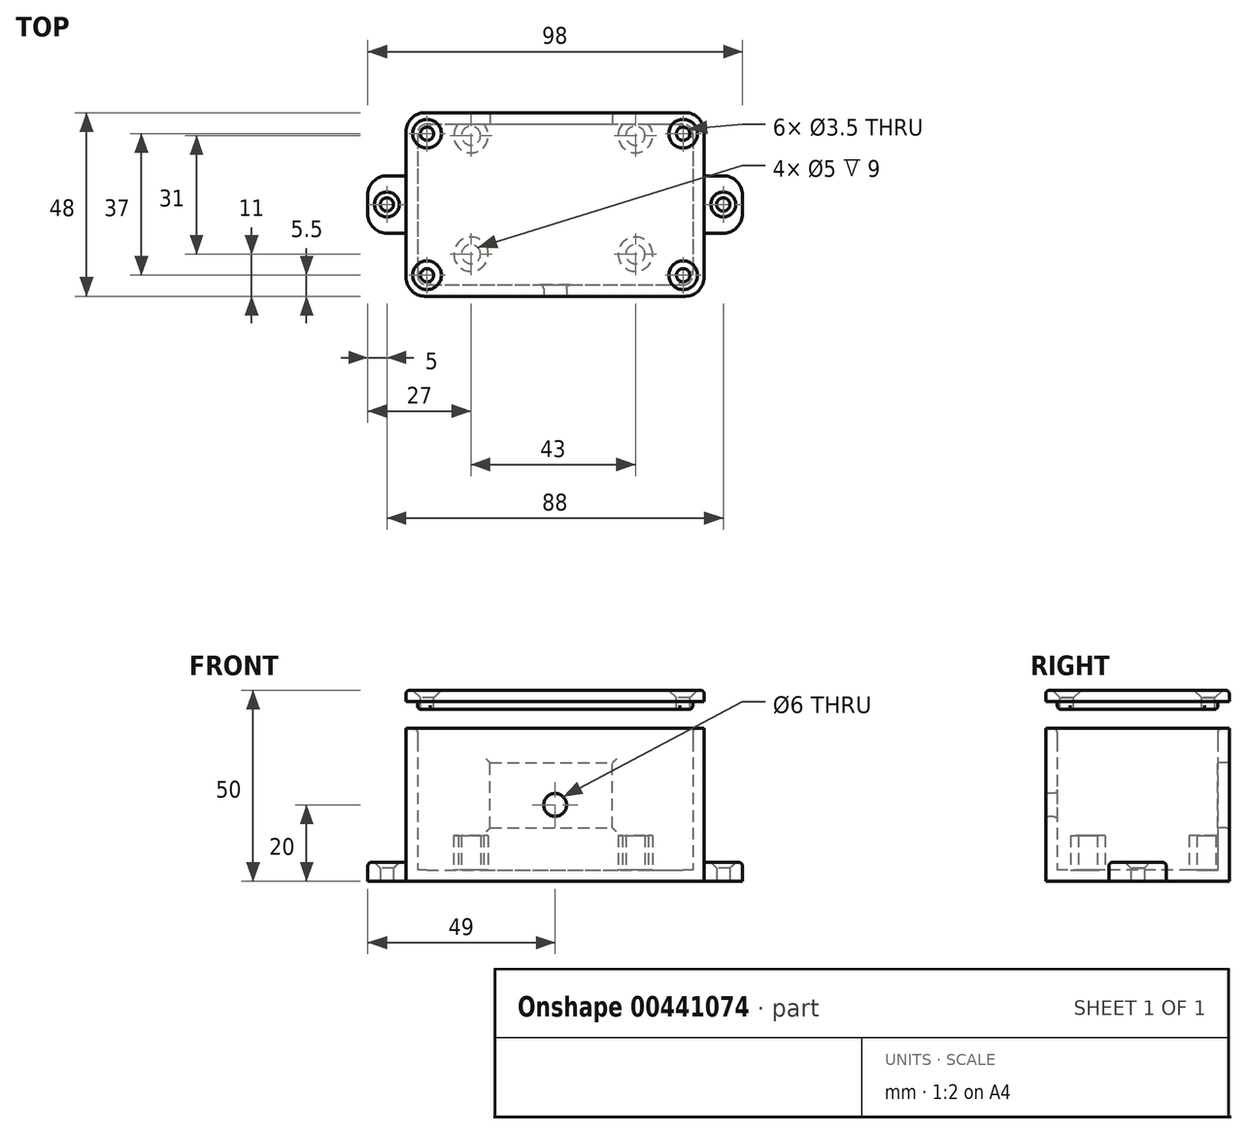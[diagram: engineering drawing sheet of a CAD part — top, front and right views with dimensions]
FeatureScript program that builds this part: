
annotation { "Feature Type Name" : "Feature", "Feature Type Description" : "" }
export const myFeature = defineFeature(function(context is Context, id is Id, definition is map)
    precondition{}
    {
        {
            var Q0;
            Q0=qCreatedBy(makeId("Top.planeOp"),FACE);
            var sketch = newSketch(context, id + "F0", { "sketchPlane" : qUnion([Q0])});
            skLineSegment(sketch, "E0.bottom", {"start": v(-36, 21) * mm, "end": v(36, 21) * mm});
            skLineSegment(sketch, "E0.top", {"start": v(-36, -21) * mm, "end": v(36, -21) * mm});
            skLineSegment(sketch, "E0.left", {"start": v(-36, 21) * mm, "end": v(-36, -21) * mm});
            skLineSegment(sketch, "E0.right", {"start": v(36, 21) * mm, "end": v(36, -21) * mm});
            skLineSegment(sketch, "E1.0", {"start": v(-39, 24) * mm, "end": v(39, 24) * mm});
            skLineSegment(sketch, "E1.1", {"start": v(-39, 24) * mm, "end": v(-39, -24) * mm});
            skLineSegment(sketch, "E1.2", {"start": v(-39, -24) * mm, "end": v(39, -24) * mm});
            skLineSegment(sketch, "E1.3", {"start": v(39, 24) * mm, "end": v(39, -24) * mm});
            skLineSegment(sketch, "E2.bottom", {"start": v(39, 7.5) * mm, "end": v(49, 7.5) * mm});
            skLineSegment(sketch, "E2.top", {"start": v(39, -7.5) * mm, "end": v(49, -7.5) * mm});
            skLineSegment(sketch, "E2.left", {"start": v(39, 7.5) * mm, "end": v(39, -7.5) * mm});
            skLineSegment(sketch, "E2.right", {"start": v(49, 7.5) * mm, "end": v(49, -7.5) * mm});
            skLineSegment(sketch, "E3.bottom", {"start": v(-39, -7.5) * mm, "end": v(-49, -7.5) * mm});
            skLineSegment(sketch, "E3.top", {"start": v(-39, 7.5) * mm, "end": v(-49, 7.5) * mm});
            skLineSegment(sketch, "E3.left", {"start": v(-39, -7.5) * mm, "end": v(-39, 7.5) * mm});
            skLineSegment(sketch, "E3.right", {"start": v(-49, -7.5) * mm, "end": v(-49, 7.5) * mm});
            skCircle(sketch, "E4", {"center": v(44, 0) * mm, "radius": 1.75 * mm});
            skCircle(sketch, "E5", {"center": v(-44, 0) * mm, "radius": 1.75 * mm});
            skSolve(sketch);
        }
        {
            var Q0;
            Q0=makeQuery(id+"F0.imprint","IMPRINT",FACE,{"disambiguationData":[TD([[makeQuery(id+"F0.imprint","IMPRINT",EDGE,{"derivedFrom":sQuery(id+"F0.wireOp",EDGE,"E0.bottom")}),1.0]])]});
            extrude(context, id + "F1", {"entities" : qUnion([Q0]), "depth" : 40 * mm});
        }
        {
            var Q0;
            Q0=makeQuery(id+"F0.imprint","IMPRINT",FACE,{"disambiguationData":[TD([[makeQuery(id+"F0.imprint","IMPRINT",EDGE,{"derivedFrom":sQuery(id+"F0.wireOp",EDGE,"E0.bottom")}),-1.0]])]});
            extrude(context, id + "F2", {"entities" : qUnion([Q0]), "operationType" : NewBodyOperationType.ADD, "depth" : 3 * mm});
        }
        {
            var Q0;
            Q0=makeQuery(id+"F2.opExtrude","CAP_FACE",FACE,{"disambiguationData":[OSD([sQuery(id+"F0.wireOp",EDGE,"E0.bottom"),sQuery(id+"F0.wireOp",EDGE,"E0.top"),sQuery(id+"F0.wireOp",EDGE,"E0.left"),sQuery(id+"F0.wireOp",EDGE,"E0.right")])],"isStart":false});
            var sketch = newSketch(context, id + "F3", { "sketchPlane" : qUnion([Q0])});
            skCircle(sketch, "E6", {"center": v(-22, 18) * mm, "radius": 4.5 * mm});
            skCircle(sketch, "E7", {"center": v(21, 18) * mm, "radius": 4.5 * mm});
            skCircle(sketch, "E8", {"center": v(-22, -13) * mm, "radius": 4.5 * mm});
            skCircle(sketch, "E9", {"center": v(21, -13) * mm, "radius": 4.5 * mm});
            skCircle(sketch, "E10", {"center": v(-22, 18) * mm, "radius": 2.5 * mm});
            skCircle(sketch, "E11", {"center": v(21, 18) * mm, "radius": 2.5 * mm});
            skCircle(sketch, "E12", {"center": v(-22, -13) * mm, "radius": 2.5 * mm});
            skCircle(sketch, "E13", {"center": v(21, -13) * mm, "radius": 2.5 * mm});
            skCircle(sketch, "E14", {"center": v(-33.5, 18.5) * mm, "radius": 2.5 * mm});
            skCircle(sketch, "E15", {"center": v(-33.5, -18.5) * mm, "radius": 2.5 * mm});
            skCircle(sketch, "E16", {"center": v(33.5, -18.5) * mm, "radius": 2.5 * mm});
            skCircle(sketch, "E17", {"center": v(33.5, 18.5) * mm, "radius": 2.5 * mm});
            skCircle(sketch, "E18", {"center": v(-33.5, 18.5) * mm, "radius": 5.5 * mm});
            skCircle(sketch, "E19", {"center": v(33.5, 18.5) * mm, "radius": 5.5 * mm});
            skCircle(sketch, "E20", {"center": v(33.5, -18.5) * mm, "radius": 5.5 * mm});
            skCircle(sketch, "E21", {"center": v(-33.5, -18.5) * mm, "radius": 5.5 * mm});
            skSolve(sketch);
        }
        {
            var Q0;
            Q0=makeQuery(id+"F3.imprint","IMPRINT",FACE,{"disambiguationData":[TD([[makeQuery(id+"F3.imprint","IMPRINT",EDGE,{"derivedFrom":sQuery(id+"F3.wireOp",EDGE,"E10")}),-1.0]])]});
            var Q1;
            Q1=makeQuery(id+"F3.imprint","IMPRINT",FACE,{"disambiguationData":[TD([[makeQuery(id+"F3.imprint","IMPRINT",EDGE,{"derivedFrom":sQuery(id+"F3.wireOp",EDGE,"E8")}),1.0]])]});
            var Q2;
            Q2=makeQuery(id+"F3.imprint","IMPRINT",FACE,{"disambiguationData":[TD([[makeQuery(id+"F3.imprint","IMPRINT",EDGE,{"derivedFrom":sQuery(id+"F3.wireOp",EDGE,"E9")}),1.0]])]});
            var Q3;
            Q3=makeQuery(id+"F3.imprint","IMPRINT",FACE,{"disambiguationData":[TD([[makeQuery(id+"F3.imprint","IMPRINT",EDGE,{"derivedFrom":sQuery(id+"F3.wireOp",EDGE,"E11")}),-1.0]])]});
            var Q4;
            Q4=makeQuery(id+"F3.imprint","IMPRINT",FACE,{"disambiguationData":[TD([[makeQuery(id+"F3.imprint","IMPRINT",EDGE,{"derivedFrom":sQuery(id+"F3.wireOp",EDGE,"E12")}),-1.0]])]});
            extrude(context, id + "F4", {"entities" : qUnion([Q0, Q1, Q2, Q3, Q4]), "operationType" : NewBodyOperationType.ADD, "depth" : 9 * mm});
        }
        {
            var Q0;
            Q0=makeQuery(id+"F1.opExtrude","SWEPT_FACE",FACE,{"disambiguationData":[OSD([sQuery(id+"F0.wireOp",EDGE,"E0.bottom")])]});
            var sketch = newSketch(context, id + "F5", { "sketchPlane" : qUnion([Q0])});
            skLineSegment(sketch, "E22.bottom", {"start": v(-17, 14) * mm, "end": v(15, 14) * mm});
            skLineSegment(sketch, "E22.top", {"start": v(-17, 31) * mm, "end": v(15, 31) * mm});
            skLineSegment(sketch, "E22.left", {"start": v(-17, 14) * mm, "end": v(-17, 31) * mm});
            skLineSegment(sketch, "E22.right", {"start": v(15, 14) * mm, "end": v(15, 31) * mm});
            skSolve(sketch);
        }
        {
            var Q0;
            Q0=makeQuery(id+"F5.imprint","IMPRINT",FACE,{"disambiguationData":[TD([[makeQuery(id+"F5.imprint","IMPRINT",EDGE,{"derivedFrom":sQuery(id+"F5.wireOp",EDGE,"E22.bottom")}),1.0]])]});
            extrude(context, id + "F6", {"entities" : qUnion([Q0]), "operationType" : NewBodyOperationType.REMOVE, "oppositeDirection" : true, "depth" : 25 * mm});
        }
        {
            var Q0;
            {var subQ0=sQuery(id+"F3.wireOp",EDGE,"E15");var subQ1=makeQuery(id+"F2.opExtrude","CAP_EDGE",EDGE,{"disambiguationData":[OSD([sQuery(id+"F0.wireOp",EDGE,"E0.top")])],"isStart":false});var subQ2=makeQuery(id+"F3.imprint","INTERSECT",VERTEX,{"derivedFrom":[subQ1,subQ0]});Q0=makeQuery(id+"F3.imprint","IMPRINT",FACE,{"disambiguationData":[TD([[makeQuery(id+"F3.imprint","IMPRINT",EDGE,{"disambiguationData":[TD([[subQ2,-1.0]])],"derivedFrom":subQ0}),-1.0]])]});}
            var Q1;
            {var subQ0=sQuery(id+"F3.wireOp",EDGE,"E16");var subQ1=makeQuery(id+"F2.opExtrude","CAP_EDGE",EDGE,{"disambiguationData":[OSD([sQuery(id+"F0.wireOp",EDGE,"E0.top")])],"isStart":false});var subQ2=makeQuery(id+"F3.imprint","INTERSECT",VERTEX,{"derivedFrom":[subQ1,subQ0]});Q1=makeQuery(id+"F3.imprint","IMPRINT",FACE,{"disambiguationData":[TD([[makeQuery(id+"F3.imprint","IMPRINT",EDGE,{"disambiguationData":[TD([[subQ2,1.0]])],"derivedFrom":subQ0}),-1.0]])]});}
            var Q2;
            {var subQ0=sQuery(id+"F3.wireOp",EDGE,"E17");var subQ1=makeQuery(id+"F2.opExtrude","CAP_EDGE",EDGE,{"disambiguationData":[OSD([sQuery(id+"F0.wireOp",EDGE,"E0.bottom")])],"isStart":false});var subQ2=makeQuery(id+"F3.imprint","INTERSECT",VERTEX,{"derivedFrom":[subQ1,subQ0]});Q2=makeQuery(id+"F3.imprint","IMPRINT",FACE,{"disambiguationData":[TD([[makeQuery(id+"F3.imprint","IMPRINT",EDGE,{"disambiguationData":[TD([[subQ2,-1.0]])],"derivedFrom":subQ0}),-1.0]])]});}
            var Q3;
            {var subQ0=sQuery(id+"F3.wireOp",EDGE,"E14");var subQ1=makeQuery(id+"F2.opExtrude","CAP_EDGE",EDGE,{"disambiguationData":[OSD([sQuery(id+"F0.wireOp",EDGE,"E0.bottom")])],"isStart":false});var subQ2=makeQuery(id+"F3.imprint","INTERSECT",VERTEX,{"derivedFrom":[subQ1,subQ0]});Q3=makeQuery(id+"F3.imprint","IMPRINT",FACE,{"disambiguationData":[TD([[makeQuery(id+"F3.imprint","IMPRINT",EDGE,{"disambiguationData":[TD([[subQ2,1.0]])],"derivedFrom":subQ0}),-1.0]])]});}
            extrude(context, id + "F7", {"entities" : qUnion([Q0, Q1, Q2, Q3]), "operationType" : NewBodyOperationType.ADD, "depth" : 34 * mm});
        }
        {
            var Q0;
            Q0=makeQuery(id+"F1.opExtrude","SWEPT_EDGE",EDGE,{"disambiguationData":[OSD([sQuery(id+"F0.wireOp",EDGE,"E1.1"),sQuery(id+"F0.wireOp",EDGE,"E1.2")])]});
            var Q1;
            Q1=makeQuery(id+"F1.opExtrude","SWEPT_EDGE",EDGE,{"disambiguationData":[OSD([sQuery(id+"F0.wireOp",EDGE,"E1.2"),sQuery(id+"F0.wireOp",EDGE,"E1.3")])]});
            var Q2;
            Q2=makeQuery(id+"F1.opExtrude","SWEPT_EDGE",EDGE,{"disambiguationData":[OSD([sQuery(id+"F0.wireOp",EDGE,"E1.0"),sQuery(id+"F0.wireOp",EDGE,"E1.3")])]});
            var Q3;
            Q3=makeQuery(id+"F1.opExtrude","SWEPT_EDGE",EDGE,{"disambiguationData":[OSD([sQuery(id+"F0.wireOp",EDGE,"E1.0"),sQuery(id+"F0.wireOp",EDGE,"E1.1")])]});
            fillet(context, id + "F8", {"entities" : qUnion([Q0, Q1, Q2, Q3]), "radius" : 5 * mm, "tangentPropagation" : true, "allowEdgeOverflow" : false});
        }
        {
            var Q0;
            Q0=makeQuery(id+"F1.opExtrude","SWEPT_EDGE",EDGE,{"disambiguationData":[OSD([sQuery(id+"F0.wireOp",EDGE,"E0.top"),sQuery(id+"F0.wireOp",EDGE,"E0.left")])]});
            var Q1;
            Q1=makeQuery(id+"F1.opExtrude","SWEPT_EDGE",EDGE,{"disambiguationData":[OSD([sQuery(id+"F0.wireOp",EDGE,"E0.bottom"),sQuery(id+"F0.wireOp",EDGE,"E0.left")])]});
            var Q2;
            Q2=makeQuery(id+"F1.opExtrude","SWEPT_EDGE",EDGE,{"disambiguationData":[OSD([sQuery(id+"F0.wireOp",EDGE,"E0.top"),sQuery(id+"F0.wireOp",EDGE,"E0.right")])]});
            var Q3;
            Q3=makeQuery(id+"F1.opExtrude","SWEPT_EDGE",EDGE,{"disambiguationData":[OSD([sQuery(id+"F0.wireOp",EDGE,"E0.bottom"),sQuery(id+"F0.wireOp",EDGE,"E0.right")])]});
            fillet(context, id + "F9", {"entities" : qUnion([Q0, Q1, Q2, Q3]), "radius" : 2.5 * mm, "tangentPropagation" : true, "allowEdgeOverflow" : false});
        }
        {
            var Q0;
            Q0=makeQuery(id+"F6.boolean.opBoolean","INTERSECT",EDGE,{"derivedFrom":[makeQuery(id+"F1.opExtrude","SWEPT_FACE",FACE,{"disambiguationData":[OSD([sQuery(id+"F0.wireOp",EDGE,"E1.0")])]}),makeQuery(id+"F6.opExtrude","SWEPT_FACE",FACE,{"disambiguationData":[OSD([sQuery(id+"F5.wireOp",EDGE,"E22.top")])]})]});
            var Q1;
            Q1=makeQuery(id+"F6.boolean.opBoolean","INTERSECT",EDGE,{"derivedFrom":[makeQuery(id+"F1.opExtrude","SWEPT_FACE",FACE,{"disambiguationData":[OSD([sQuery(id+"F0.wireOp",EDGE,"E1.0")])]}),makeQuery(id+"F6.opExtrude","SWEPT_FACE",FACE,{"disambiguationData":[OSD([sQuery(id+"F5.wireOp",EDGE,"E22.left")])]})]});
            var Q2;
            Q2=makeQuery(id+"F6.boolean.opBoolean","INTERSECT",EDGE,{"derivedFrom":[makeQuery(id+"F1.opExtrude","SWEPT_FACE",FACE,{"disambiguationData":[OSD([sQuery(id+"F0.wireOp",EDGE,"E1.0")])]}),makeQuery(id+"F6.opExtrude","SWEPT_FACE",FACE,{"disambiguationData":[OSD([sQuery(id+"F5.wireOp",EDGE,"E22.bottom")])]})]});
            var Q3;
            Q3=makeQuery(id+"F6.boolean.opBoolean","INTERSECT",EDGE,{"derivedFrom":[makeQuery(id+"F1.opExtrude","SWEPT_FACE",FACE,{"disambiguationData":[OSD([sQuery(id+"F0.wireOp",EDGE,"E1.0")])]}),makeQuery(id+"F6.opExtrude","SWEPT_FACE",FACE,{"disambiguationData":[OSD([sQuery(id+"F5.wireOp",EDGE,"E22.right")])]})]});
            fillet(context, id + "F10", {"entities" : qUnion([Q0, Q1, Q2, Q3]), "radius" : 1 * mm, "tangentPropagation" : true, "allowEdgeOverflow" : false});
        }
        {
            var Q0;
            Q0=makeQuery(id+"F0.imprint","IMPRINT",FACE,{"disambiguationData":[TD([[makeQuery(id+"F0.imprint","IMPRINT",EDGE,{"derivedFrom":sQuery(id+"F0.wireOp",EDGE,"E2.bottom")}),-1.0]])]});
            var Q1;
            Q1=makeQuery(id+"F0.imprint","IMPRINT",FACE,{"disambiguationData":[TD([[makeQuery(id+"F0.imprint","IMPRINT",EDGE,{"derivedFrom":sQuery(id+"F0.wireOp",EDGE,"E3.bottom")}),-1.0]])]});
            extrude(context, id + "F11", {"entities" : qUnion([Q0, Q1]), "operationType" : NewBodyOperationType.ADD, "depth" : 5 * mm});
        }
        {
            var Q0;
            Q0=makeQuery(id+"F11.opExtrude","SWEPT_EDGE",EDGE,{"disambiguationData":[OSD([sQuery(id+"F0.wireOp",EDGE,"E2.bottom"),sQuery(id+"F0.wireOp",EDGE,"E2.right")])]});
            var Q1;
            Q1=makeQuery(id+"F11.opExtrude","SWEPT_EDGE",EDGE,{"disambiguationData":[OSD([sQuery(id+"F0.wireOp",EDGE,"E3.top"),sQuery(id+"F0.wireOp",EDGE,"E3.right")])]});
            var Q2;
            Q2=makeQuery(id+"F11.opExtrude","SWEPT_EDGE",EDGE,{"disambiguationData":[OSD([sQuery(id+"F0.wireOp",EDGE,"E3.bottom"),sQuery(id+"F0.wireOp",EDGE,"E3.right")])]});
            var Q3;
            Q3=makeQuery(id+"F11.opExtrude","SWEPT_EDGE",EDGE,{"disambiguationData":[OSD([sQuery(id+"F0.wireOp",EDGE,"E2.top"),sQuery(id+"F0.wireOp",EDGE,"E2.right")])]});
            fillet(context, id + "F12", {"entities" : qUnion([Q0, Q1, Q2, Q3]), "radius" : 5 * mm, "tangentPropagation" : true, "allowEdgeOverflow" : false});
        }
        {
            var Q0;
            Q0=makeQuery(id+"F11.opExtrude","CAP_EDGE",EDGE,{"disambiguationData":[OSD([sQuery(id+"F0.wireOp",EDGE,"E3.top")])],"isStart":false});
            var Q1;
            Q1=makeQuery(id+"F11.opExtrude","CAP_EDGE",EDGE,{"disambiguationData":[OSD([sQuery(id+"F0.wireOp",EDGE,"E2.top")])],"isStart":false});
            fillet(context, id + "F13", {"entities" : qUnion([Q0, Q1]), "radius" : 1 * mm, "tangentPropagation" : true, "allowEdgeOverflow" : false});
        }
        {
            var Q0;
            Q0=makeQuery(id+"F11.opExtrude","CAP_EDGE",EDGE,{"disambiguationData":[OSD([sQuery(id+"F0.wireOp",EDGE,"E4")])],"isStart":false});
            var Q1;
            Q1=makeQuery(id+"F11.opExtrude","CAP_EDGE",EDGE,{"disambiguationData":[OSD([sQuery(id+"F0.wireOp",EDGE,"E5")])],"isStart":false});
            chamfer(context, id + "F14", {"entities" : qUnion([Q0, Q1]), "width" : 1.5 * mm, "tangentPropagation" : true});
        }
        {
            var Q0;
            Q0=qCreatedBy(makeId("Top.planeOp"),FACE);
            cPlane(context, id + "F15", {"entities" : qUnion([Q0]), "cplaneType" : CPlaneType.OFFSET, "offset" : 50 * mm, "width" : 150 * mm, "height" : 150 * mm});
        }
        {
            var Q0;
            Q0=qCreatedBy(id+"F15.planeOp",FACE);
            var sketch = newSketch(context, id + "F16", { "sketchPlane" : qUnion([Q0])});
            skLineSegment(sketch, "E23.bottom", {"start": v(-39, 24) * mm, "end": v(39, 24) * mm});
            skLineSegment(sketch, "E23.top", {"start": v(-39, -24) * mm, "end": v(39, -24) * mm});
            skLineSegment(sketch, "E23.left", {"start": v(-39, 24) * mm, "end": v(-39, -24) * mm});
            skLineSegment(sketch, "E23.right", {"start": v(39, 24) * mm, "end": v(39, -24) * mm});
            skCircle(sketch, "E24", {"center": v(-33.5, 18.5) * mm, "radius": 1.75 * mm});
            skCircle(sketch, "E25.MirrorC", {"center": v(33.5, 18.5) * mm, "radius": 1.75 * mm});
            skCircle(sketch, "E26.MirrorC", {"center": v(-33.5, -18.5) * mm, "radius": 1.75 * mm});
            skCircle(sketch, "E27.MirrorC", {"center": v(33.5, -18.5) * mm, "radius": 1.75 * mm});
            skLineSegment(sketch, "E28.bottom", {"start": v(-36, 21) * mm, "end": v(36, 21) * mm});
            skLineSegment(sketch, "E28.top", {"start": v(-36, -21) * mm, "end": v(36, -21) * mm});
            skLineSegment(sketch, "E28.left", {"start": v(-36, 21) * mm, "end": v(-36, -21) * mm});
            skLineSegment(sketch, "E28.right", {"start": v(36, 21) * mm, "end": v(36, -21) * mm});
            skSolve(sketch);
        }
        {
            var Q0;
            Q0=makeQuery(id+"F16.imprint","IMPRINT",FACE,{"disambiguationData":[TD([[makeQuery(id+"F16.imprint","IMPRINT",EDGE,{"derivedFrom":sQuery(id+"F16.wireOp",EDGE,"E23.bottom")}),-1.0]])]});
            extrude(context, id + "F17", {"entities" : qUnion([Q0]), "oppositeDirection" : true, "depth" : 3 * mm});
        }
        {
            var Q0;
            Q0=makeQuery(id+"F16.imprint","IMPRINT",FACE,{"disambiguationData":[TD([[makeQuery(id+"F16.imprint","IMPRINT",EDGE,{"derivedFrom":sQuery(id+"F16.wireOp",EDGE,"E24")}),-1.0]])]});
            extrude(context, id + "F18", {"entities" : qUnion([Q0]), "operationType" : NewBodyOperationType.ADD, "oppositeDirection" : true, "depth" : 5 * mm});
        }
        {
            var Q0;
            Q0=makeQuery(id+"F18.opExtrude","CAP_EDGE",EDGE,{"disambiguationData":[OSD([sQuery(id+"F16.wireOp",EDGE,"E24")])],"isStart":true});
            var Q1;
            Q1=makeQuery(id+"F18.opExtrude","CAP_EDGE",EDGE,{"disambiguationData":[OSD([sQuery(id+"F16.wireOp",EDGE,"E26.MirrorC")])],"isStart":true});
            var Q2;
            Q2=makeQuery(id+"F18.opExtrude","CAP_EDGE",EDGE,{"disambiguationData":[OSD([sQuery(id+"F16.wireOp",EDGE,"E25.MirrorC")])],"isStart":true});
            var Q3;
            Q3=makeQuery(id+"F18.opExtrude","CAP_EDGE",EDGE,{"disambiguationData":[OSD([sQuery(id+"F16.wireOp",EDGE,"E27.MirrorC")])],"isStart":true});
            chamfer(context, id + "F19", {"entities" : qUnion([Q0, Q1, Q2, Q3]), "width" : 2 * mm, "tangentPropagation" : true});
        }
        {
            var Q0;
            Q0=makeQuery(id+"F17.opExtrude","SWEPT_EDGE",EDGE,{"disambiguationData":[OSD([sQuery(id+"F16.wireOp",EDGE,"E23.top"),sQuery(id+"F16.wireOp",EDGE,"E23.left")])]});
            var Q1;
            Q1=makeQuery(id+"F17.opExtrude","SWEPT_EDGE",EDGE,{"disambiguationData":[OSD([sQuery(id+"F16.wireOp",EDGE,"E23.bottom"),sQuery(id+"F16.wireOp",EDGE,"E23.left")])]});
            var Q2;
            Q2=makeQuery(id+"F17.opExtrude","SWEPT_EDGE",EDGE,{"disambiguationData":[OSD([sQuery(id+"F16.wireOp",EDGE,"E23.bottom"),sQuery(id+"F16.wireOp",EDGE,"E23.right")])]});
            var Q3;
            Q3=makeQuery(id+"F17.opExtrude","SWEPT_EDGE",EDGE,{"disambiguationData":[OSD([sQuery(id+"F16.wireOp",EDGE,"E23.top"),sQuery(id+"F16.wireOp",EDGE,"E23.right")])]});
            fillet(context, id + "F20", {"entities" : qUnion([Q0, Q1, Q2, Q3]), "radius" : 5 * mm, "tangentPropagation" : true, "allowEdgeOverflow" : false});
        }
        {
            var Q0;
            Q0=makeQuery(id+"F18.opExtrude","SWEPT_EDGE",EDGE,{"disambiguationData":[OSD([sQuery(id+"F16.wireOp",EDGE,"E28.top"),sQuery(id+"F16.wireOp",EDGE,"E28.right")])]});
            var Q1;
            Q1=makeQuery(id+"F18.opExtrude","SWEPT_EDGE",EDGE,{"disambiguationData":[OSD([sQuery(id+"F16.wireOp",EDGE,"E28.bottom"),sQuery(id+"F16.wireOp",EDGE,"E28.right")])]});
            var Q2;
            Q2=makeQuery(id+"F18.opExtrude","SWEPT_EDGE",EDGE,{"disambiguationData":[OSD([sQuery(id+"F16.wireOp",EDGE,"E28.bottom"),sQuery(id+"F16.wireOp",EDGE,"E28.left")])]});
            var Q3;
            Q3=makeQuery(id+"F18.opExtrude","SWEPT_EDGE",EDGE,{"disambiguationData":[OSD([sQuery(id+"F16.wireOp",EDGE,"E28.top"),sQuery(id+"F16.wireOp",EDGE,"E28.left")])]});
            fillet(context, id + "F21", {"entities" : qUnion([Q0, Q1, Q2, Q3]), "radius" : 2.5 * mm, "tangentPropagation" : true, "allowEdgeOverflow" : false});
        }
        {
            var Q0;
            Q0=makeQuery(id+"F17.opExtrude","CAP_EDGE",EDGE,{"disambiguationData":[OSD([sQuery(id+"F16.wireOp",EDGE,"E23.right")])],"isStart":true});
            fillet(context, id + "F22", {"entities" : qUnion([Q0]), "radius" : 1 * mm, "tangentPropagation" : true, "allowEdgeOverflow" : false});
        }
        {
            var Q0;
            Q0=makeQuery(id+"F1.opExtrude","SWEPT_FACE",FACE,{"disambiguationData":[OSD([sQuery(id+"F0.wireOp",EDGE,"E1.2")])]});
            var sketch = newSketch(context, id + "F23", { "sketchPlane" : qUnion([Q0])});
            skCircle(sketch, "E29", {"center": v(0, 20) * mm, "radius": 3 * mm});
            skPoint(sketch, "E29.centerSnap0", {"position": v(-34, 20) * mm});
            skPoint(sketch, "E29.centerSnap1", {"position": v(0, 40) * mm});
            skSolve(sketch);
        }
        {
            var Q0;
            Q0=makeQuery(id+"F23.imprint","IMPRINT",FACE,{"disambiguationData":[TD([[makeQuery(id+"F23.imprint","IMPRINT",EDGE,{"derivedFrom":sQuery(id+"F23.wireOp",EDGE,"E29")}),1.0]])]});
            extrude(context, id + "F24", {"entities" : qUnion([Q0]), "operationType" : NewBodyOperationType.REMOVE, "oppositeDirection" : true, "depth" : 25 * mm});
        }
        {
            var Q0;
            Q0=makeQuery(id+"F24.boolean.opBoolean","COPY",EDGE,{"derivedFrom":makeQuery(id+"F24.opExtrude","CAP_EDGE",EDGE,{"disambiguationData":[OSD([sQuery(id+"F23.wireOp",EDGE,"E29")])],"isStart":true})});
            var Q1;
            Q1=makeQuery(id+"F24.boolean.opBoolean","INTERSECT",EDGE,{"derivedFrom":[makeQuery(id+"F1.opExtrude","SWEPT_FACE",FACE,{"disambiguationData":[OSD([sQuery(id+"F0.wireOp",EDGE,"E0.top")])]}),makeQuery(id+"F24.opExtrude","SWEPT_FACE",FACE,{"disambiguationData":[OSD([sQuery(id+"F23.wireOp",EDGE,"E29")])]})]});
            fillet(context, id + "F25", {"entities" : qUnion([Q0, Q1]), "radius" : 1 * mm, "tangentPropagation" : true, "allowEdgeOverflow" : false});
        }
        {
            var Q0;
            Q0=makeQuery(id+"F18.opExtrude","CAP_EDGE",EDGE,{"disambiguationData":[OSD([sQuery(id+"F16.wireOp",EDGE,"E28.bottom")])],"isStart":false});
            fillet(context, id + "F26", {"entities" : qUnion([Q0]), "radius" : 1 * mm, "tangentPropagation" : true, "allowEdgeOverflow" : false});
        }
        {
            var Q0;
            Q0=makeQuery(id+"F1.opExtrude","CAP_EDGE",EDGE,{"disambiguationData":[OSD([sQuery(id+"F0.wireOp",EDGE,"E0.bottom")])],"isStart":false});
            fillet(context, id + "F27", {"entities" : qUnion([Q0]), "radius" : 1 * mm, "tangentPropagation" : true, "allowEdgeOverflow" : false});
        }
    });
